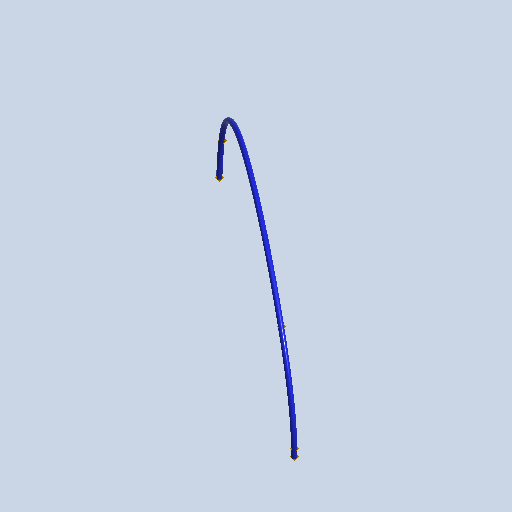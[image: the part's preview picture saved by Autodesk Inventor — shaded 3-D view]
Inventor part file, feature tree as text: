
AUTODESK INVENTOR PART (.ipt)
format: ipt  version: 2023.1 (Build 271208000, 208)  size: 109,056 bytes
history: native  units: mm (DEFAULTED — no unit token found)
features: other x7, plane x1, sketch x1, sweep x1
ambient origin geometry x8: Origin, YZ Plane, XZ Plane, XY Plane, X Axis, Y Axis, Z Axis, Center Point
bodies: Body1 (feature_tree)
feature tree (10):
  other  "Work Point1"
  other  "Work Point2"
  other  "Segment1"
  plane  "Work Plane1"
  other  "Work Point3"
  other  "Work Point4"
  other  "Work Point5"
  sketch  "Sketch1"  dims[d0=0.0mm d1=0.0mm]
  other  "Srf1"
  sweep  "SweepSrf1"
